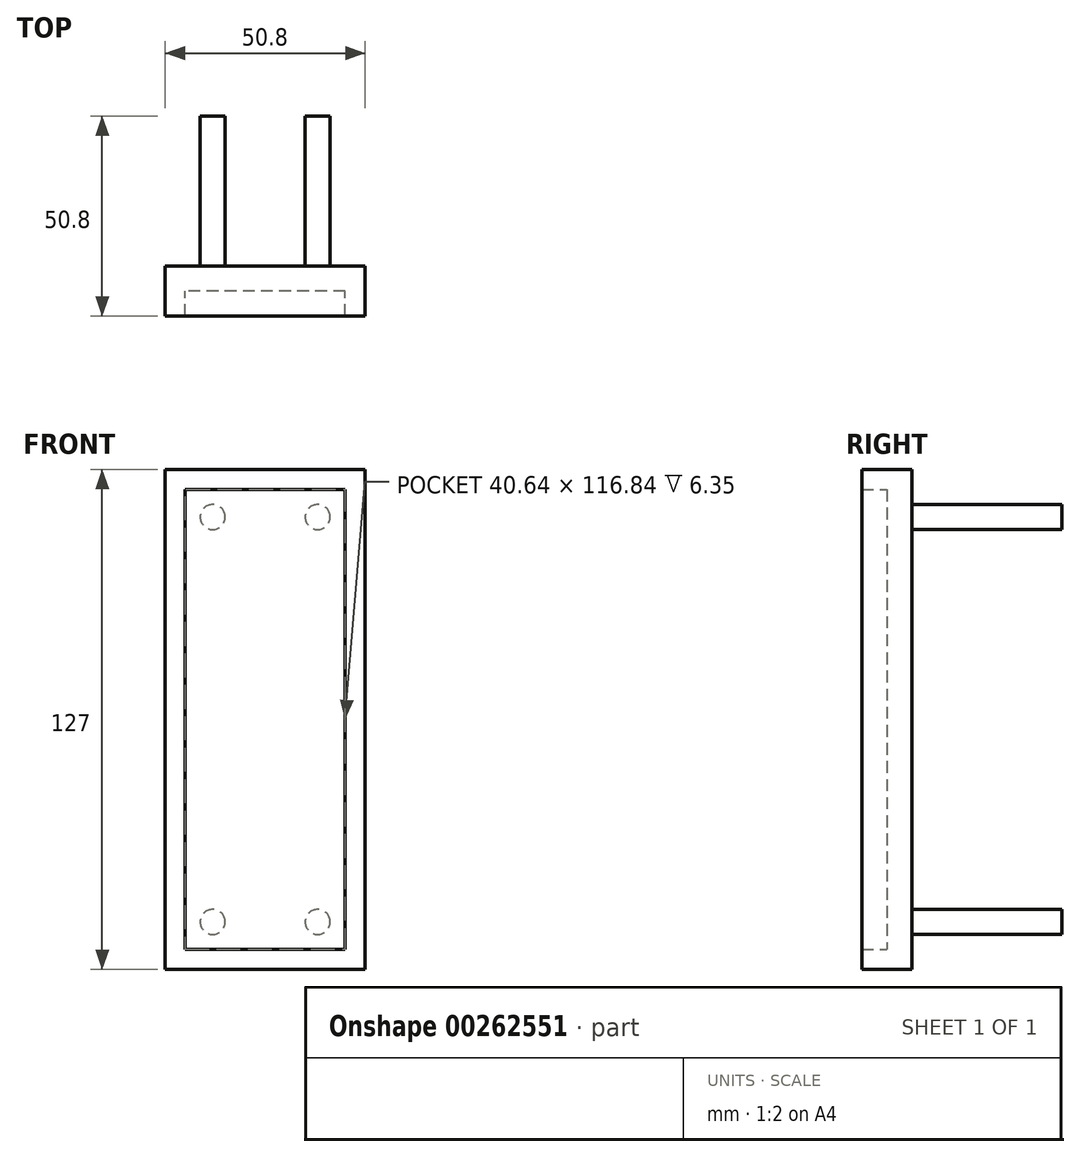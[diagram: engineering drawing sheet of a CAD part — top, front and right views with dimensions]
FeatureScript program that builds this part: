
annotation { "Feature Type Name" : "Feature", "Feature Type Description" : "" }
export const myFeature = defineFeature(function(context is Context, id is Id, definition is map)
    precondition{}
    {
        {
            var Q0;
            Q0=qCreatedBy(makeId("Front.planeOp"),FACE);
            var sketch = newSketch(context, id + "F0", { "sketchPlane" : qUnion([Q0])});
            skLineSegment(sketch, "E0.bottom", {"start": v(25.4, 63.5) * mm, "end": v(-25.4, 63.5) * mm});
            skLineSegment(sketch, "E0.top", {"start": v(25.4, -63.5) * mm, "end": v(-25.4, -63.5) * mm});
            skLineSegment(sketch, "E0.left", {"start": v(25.4, 63.5) * mm, "end": v(25.4, -63.5) * mm});
            skLineSegment(sketch, "E0.right", {"start": v(-25.4, 63.5) * mm, "end": v(-25.4, -63.5) * mm});
            skPoint(sketch, "E0.middle", {"position": v(0, 0) * mm});
            skLineSegment(sketch, "E1.bottom", {"start": v(20.32, 58.42) * mm, "end": v(-20.32, 58.42) * mm});
            skLineSegment(sketch, "E1.top", {"start": v(20.32, -58.42) * mm, "end": v(-20.32, -58.42) * mm});
            skLineSegment(sketch, "E1.left", {"start": v(20.32, 58.42) * mm, "end": v(20.32, -58.42) * mm});
            skLineSegment(sketch, "E1.right", {"start": v(-20.32, 58.42) * mm, "end": v(-20.32, -58.42) * mm});
            skSolve(sketch);
        }
        {
            var Q0;
            Q0=makeQuery(id+"F0.imprint","IMPRINT",FACE,{"disambiguationData":[TD([[makeQuery(id+"F0.imprint","IMPRINT",EDGE,{"derivedFrom":sQuery(id+"F0.wireOp",EDGE,"E1.bottom")}),1.0]])]});
            extrude(context, id + "F1", {"entities" : qUnion([Q0]), "depth" : 6.35 * mm});
        }
        {
            var Q0;
            Q0=makeQuery(id+"F0.imprint","IMPRINT",FACE,{"disambiguationData":[TD([[makeQuery(id+"F0.imprint","IMPRINT",EDGE,{"derivedFrom":sQuery(id+"F0.wireOp",EDGE,"E0.bottom")}),1.0]])]});
            extrude(context, id + "F2", {"entities" : qUnion([Q0]), "operationType" : NewBodyOperationType.ADD, "depth" : 12.7 * mm});
        }
        {
            var Q0;
            Q0=makeQuery(id+"F0.imprint","IMPRINT",FACE,{"disambiguationData":[TD([[makeQuery(id+"F0.imprint","IMPRINT",EDGE,{"derivedFrom":sQuery(id+"F0.wireOp",EDGE,"E1.bottom")}),1.0]])]});
            var sketch = newSketch(context, id + "F3", { "sketchPlane" : qUnion([Q0])});
            skCircle(sketch, "E2", {"center": v(-13.33, -51.44) * mm, "radius": 3.18 * mm});
            skCircle(sketch, "E3", {"center": v(13.34, -51.44) * mm, "radius": 3.18 * mm});
            skCircle(sketch, "E4", {"center": v(13.34, 51.43) * mm, "radius": 3.18 * mm});
            skCircle(sketch, "E5", {"center": v(-13.33, 51.43) * mm, "radius": 3.18 * mm});
            skSolve(sketch);
        }
        {
            var Q0;
            Q0 = qSketchRegion(id + "F3", true);
            extrude(context, id + "F4", {"entities" : qUnion([Q0]), "operationType" : NewBodyOperationType.ADD, "oppositeDirection" : true, "depth" : 38.1 * mm});
        }
    });
